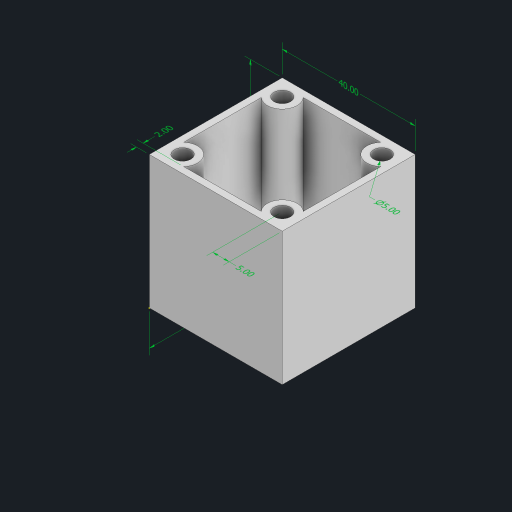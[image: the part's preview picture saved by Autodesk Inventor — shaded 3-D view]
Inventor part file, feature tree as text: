
AUTODESK INVENTOR PART (.ipt)
format: ipt  version: 2023 (Build 270158000, 158)  size: 154,624 bytes
history: native  units: in
note: dims shown in document units (in); Inventor stores cm internally (conversion verified against a paired STEP export)
features: other x8, extrude x2, sketch x2, shell x1
ambient origin geometry x8: Origin, YZ Plane, XZ Plane, XY Plane, X Axis, Y Axis, Z Axis, Center Point
bodies: Solid1 (feature_tree)
feature tree (13):
  other  "Annotations"
  extrude  "Extrusion1"  Depth=1.5748in
  extrude  "Extrusion2"  Depth=0.0787in
  shell  "Shell1"  Thickness=0.1969in
  sketch  "Sketch3"  dims[d6=1.5748in d7=0.0in d8=0.1969in d9=0.1969in d10=0.1969in d11=0.7874in d13=1.1811in d14=0.7874in d16=1.1811in d19=1.9813in d20=0.0in d21=0.0787in d24=0.0in d25=0.3937in d26=1.5748in d27=0.0in d28=0.3937in d29=1.5748in d30=0.0382in d31=0.1969in d34=1.2708in d35=0.1969in d39=0.0in d40=0.3937in d41=1.5748in d42=0.3451in d43=0.0949in d44=0.0787in]
  other  "cube_profile"
  sketch  "Sketch2"  dims[d2=1.5748in d4=1.5748in]
  other  "Linear Dimension 1"
  other  "Linear Dimension 2"
  other  "Linear Dimension 3"
  other  "Diameter Dimension 2"
  other  "Linear Dimension 4"
  other  "Linear Dimension 5"
